# Revit family: Gira_001230
name_source: partatom
category: Electrical Fixtures
revit_build: Autodesk Revit 2017 (Build: 20160225_1515(x64)
units: mm (PartAtom-declared; Revit-internal decimal feet)

## family parameters
Always vertical = Yes
Cut with Voids When Loaded = No
Maintain Annotation Orientation = No
Part Type = Normal
Room Calculation Point = No
Round Connector Dimension = Use Diameter
Shared = No
Work Plane-Based = No

## types (1)
- closure cab.entry 2-g WP SM grey
    BIM = https://media.live.bim.site
    BIMSITE_PRODUCT_ID = 8b52b8242170ea874e1da596cdf3f3d8406993a6
    Colour = Grey
    Cost = 0 $
    Description = Closure cab.entry 2g WP SM GY Seal with cable entry 2-gang (twin entry) grey Notes : - For cables  6 to 13 mm.
    GTIN = 4010337012306
    HAN = 001230
    HeinzeBIM = https://www.heinze.de
    Manufacturer = Gira
    Model = Slider with 2 inlets
    Suitable for built-up box flush-mounted switching equipment = No
    URL = https://www.gira.de

## geometry (parser evidence)
native form markers: Blend x2, Sweep x3
no freeform markers — native parametric forms only
